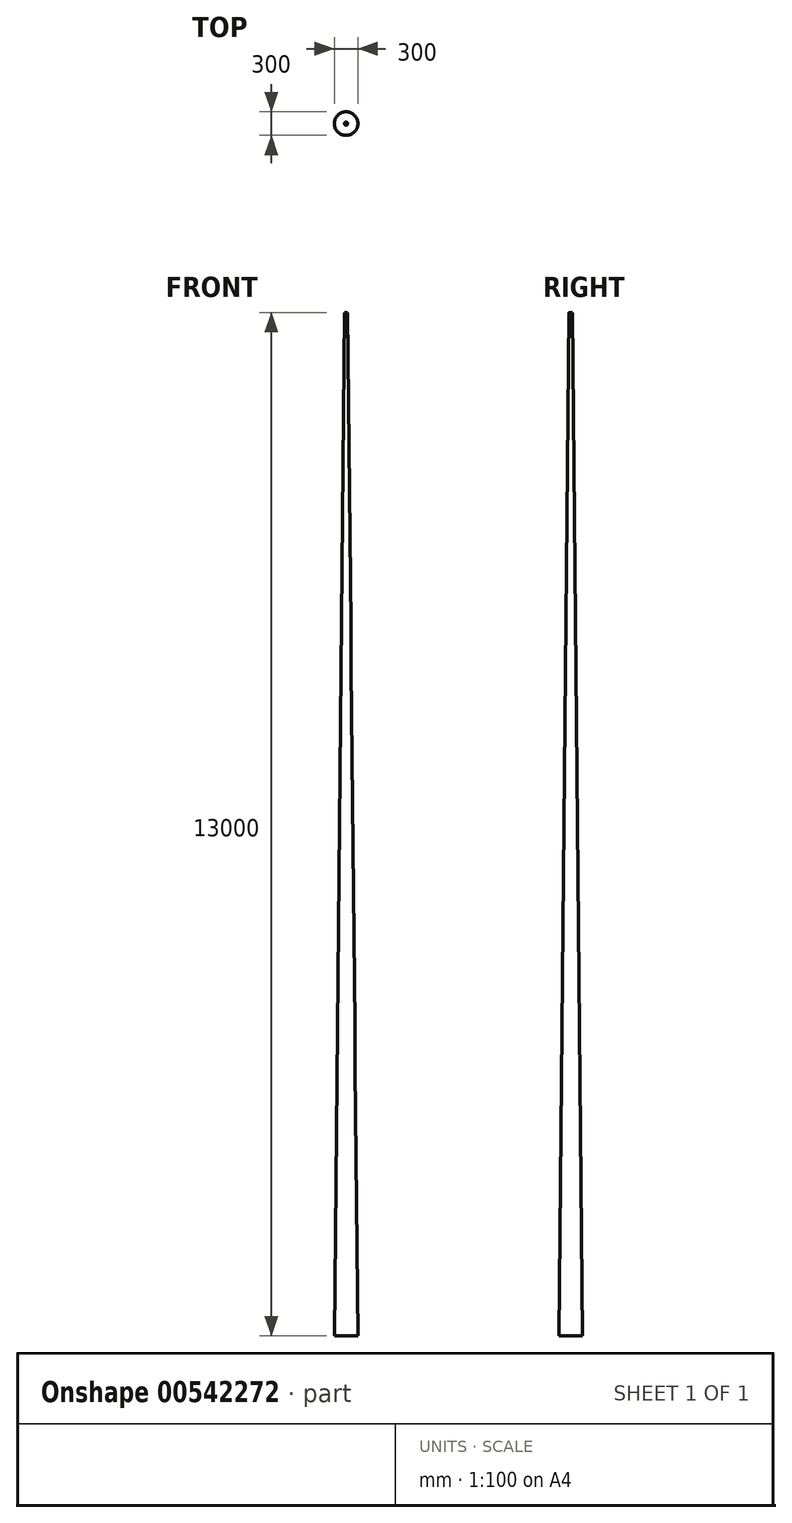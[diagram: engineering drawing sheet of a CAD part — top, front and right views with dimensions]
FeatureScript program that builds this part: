
annotation { "Feature Type Name" : "Feature", "Feature Type Description" : "" }
export const myFeature = defineFeature(function(context is Context, id is Id, definition is map)
    precondition{}
    {
        {
            var Q0;
            Q0=qCreatedBy(makeId("Right.planeOp"),FACE);
            var sketch = newSketch(context, id + "F0", { "sketchPlane" : qUnion([Q0])});
            skLineSegment(sketch, "E0", {"start": v(0, 0) * mm, "end": v(150, 0) * mm});
            skLineSegment(sketch, "E1", {"start": v(150, 0) * mm, "end": v(20, 13000) * mm});
            skLineSegment(sketch, "E2", {"start": v(20, 13000) * mm, "end": v(0, 13000) * mm});
            skLineSegment(sketch, "E3", {"start": v(0, 13000) * mm, "end": v(0, 0) * mm});
            skSolve(sketch);
        }
        {
            var Q0;
            Q0=makeQuery(id+"F0.imprint","IMPRINT",FACE,{"disambiguationData":[TD([[makeQuery(id+"F0.imprint","IMPRINT",EDGE,{"derivedFrom":sQuery(id+"F0.wireOp",EDGE,"E0")}),1.0]])]});
            var Q1;
            Q1=sQuery(id+"F0.wireOp",EDGE,"E3");
            revolve(context, id + "F1", {"entities" : qUnion([Q0]), "axis" : qUnion([Q1]), "revolveType" : RevolveType.FULL});
        }
        {
            var Q0;
            Q0=makeQuery(id+"F1.opRevolve","SWEPT_FACE",FACE,{"disambiguationData":[OSD([sQuery(id+"F0.wireOp",EDGE,"E0")])]});
            cPlane(context, id + "F2", {"entities" : qUnion([Q0]), "cplaneType" : CPlaneType.OFFSET, "offset" : 2000 * mm, "oppositeDirection" : true, "width" : 150 * mm, "height" : 150 * mm});
        }
    });
